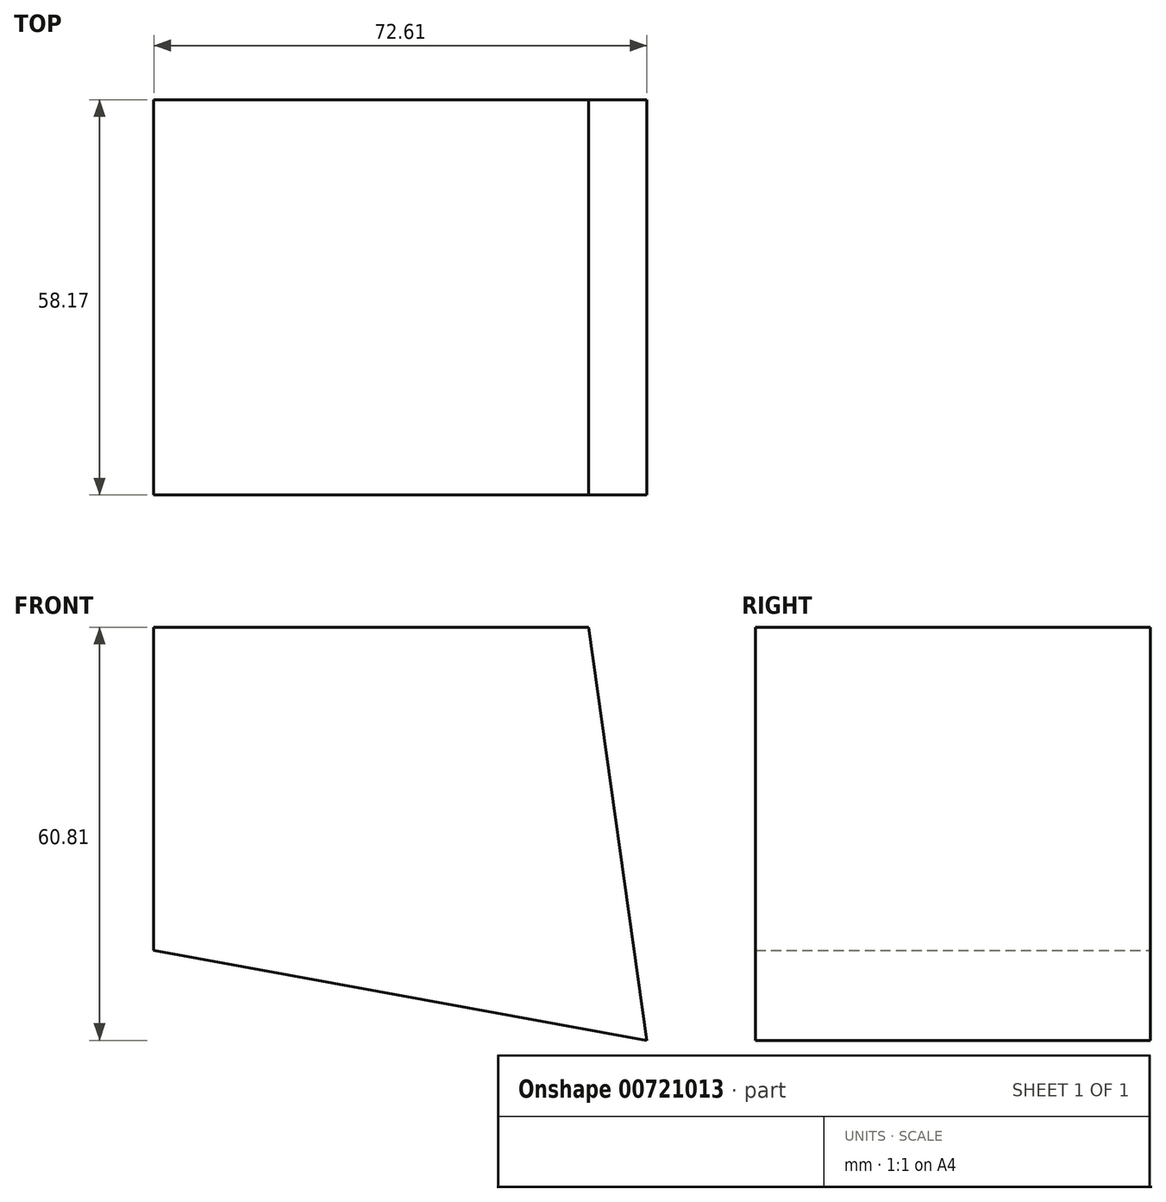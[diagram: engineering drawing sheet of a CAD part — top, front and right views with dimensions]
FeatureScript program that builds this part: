
annotation { "Feature Type Name" : "Feature", "Feature Type Description" : "" }
export const myFeature = defineFeature(function(context is Context, id is Id, definition is map)
    precondition{}
    {
        {
            var Q0;
            Q0=qCreatedBy(makeId("Front.planeOp"),FACE);
            var sketch = newSketch(context, id + "F0", { "sketchPlane" : qUnion([Q0])});
            skLineSegment(sketch, "E0", {"start": v(-23.52, -15.04) * mm, "end": v(-23.52, 32.53) * mm});
            skLineSegment(sketch, "E1", {"start": v(-23.52, 32.53) * mm, "end": v(40.5, 32.53) * mm});
            skLineSegment(sketch, "E2", {"start": v(40.5, 32.53) * mm, "end": v(49.1, -28.28) * mm});
            skLineSegment(sketch, "E3", {"start": v(49.1, -28.28) * mm, "end": v(-23.52, -15.04) * mm});
            skSolve(sketch);
        }
        {
            var Q0;
            Q0 = qSketchRegion(id + "F0", true);
            extrude(context, id + "F1", {"entities" : qUnion([Q0]), "depth" : 58.17 * mm, "offsetDistance" : 25.4 * mm});
        }
    });
